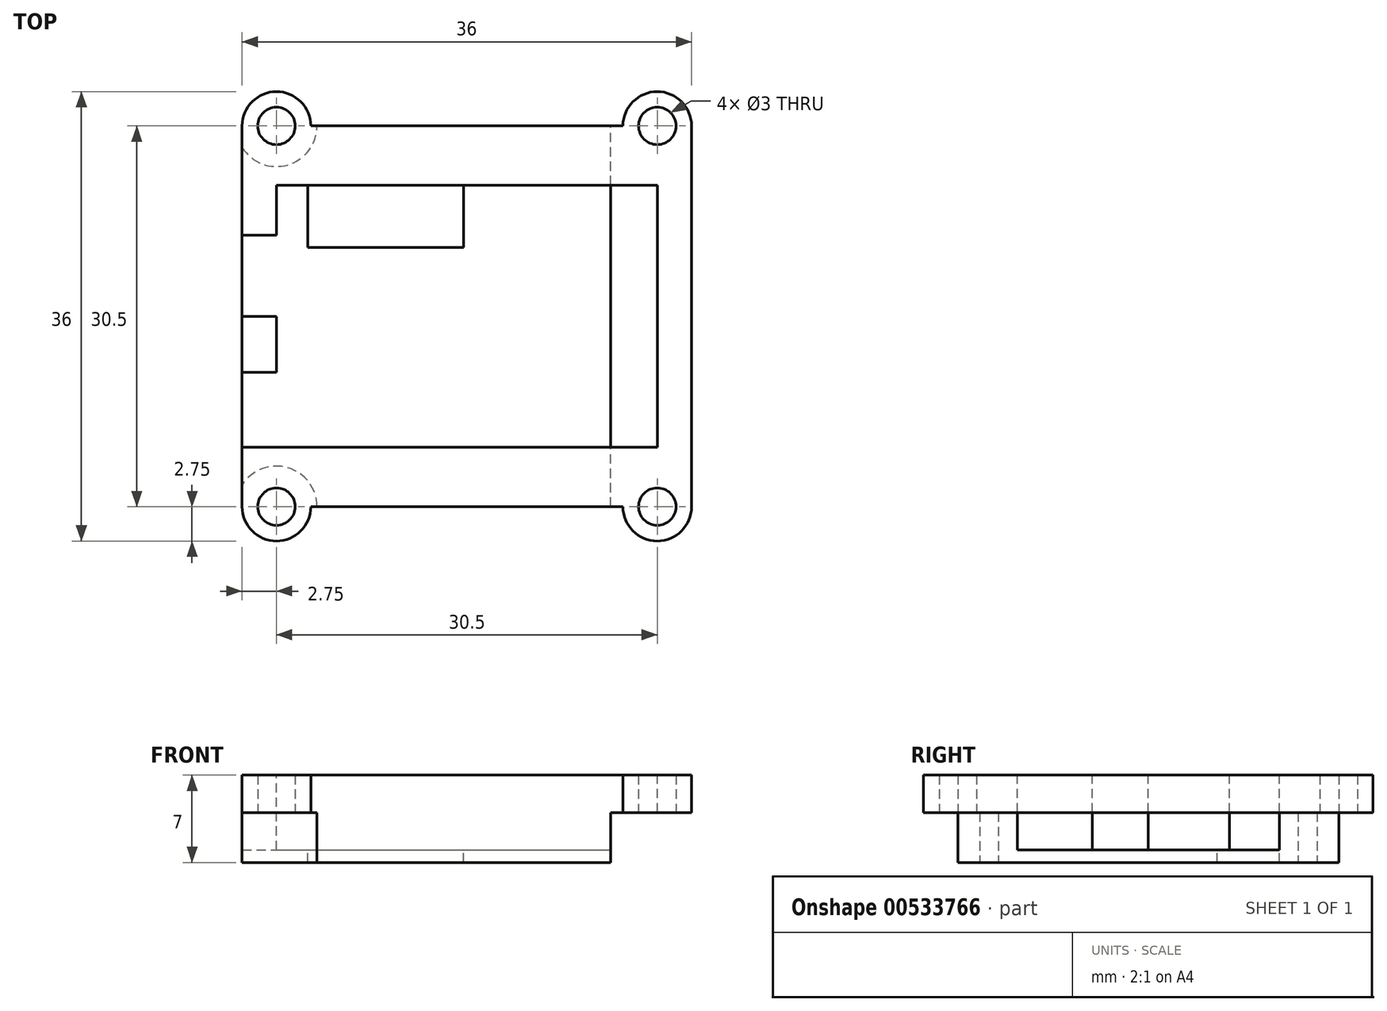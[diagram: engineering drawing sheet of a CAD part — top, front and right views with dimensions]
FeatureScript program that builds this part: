
annotation { "Feature Type Name" : "Feature", "Feature Type Description" : "" }
export const myFeature = defineFeature(function(context is Context, id is Id, definition is map)
    precondition{}
    {
        {
            var Q0;
            Q0=qCreatedBy(makeId("Top.planeOp"),FACE);
            var sketch = newSketch(context, id + "F0", { "sketchPlane" : qUnion([Q0])});
            skLineSegment(sketch, "E0.bottom", {"start": v(-18, -18) * mm, "end": v(18, -18) * mm});
            skLineSegment(sketch, "E0.top", {"start": v(-18, 18) * mm, "end": v(18, 18) * mm});
            skLineSegment(sketch, "E0.left", {"start": v(-18, -18) * mm, "end": v(-18, 18) * mm});
            skLineSegment(sketch, "E0.right", {"start": v(18, -18) * mm, "end": v(18, 18) * mm});
            skPoint(sketch, "E0.middle", {"position": v(0, 0) * mm});
            skSolve(sketch);
        }
        {
            var Q0;
            Q0=makeQuery(id+"F0.imprint","IMPRINT",FACE,{"disambiguationData":[TD([[makeQuery(id+"F0.imprint","IMPRINT",EDGE,{"derivedFrom":sQuery(id+"F0.wireOp",EDGE,"E0.bottom")}),1.0]])]});
            var Q1;
            Q1=qSketchRegion(id+"F2",true);
            extrude(context, id + "F1", {"entities" : qUnion([Q0, Q1]), "depth" : 7 * mm, "offsetDistance" : 25 * mm});
        }
        {
            var Q0;
            Q0=makeQuery(id+"F1.opExtrude","CAP_FACE",FACE,{"disambiguationData":[OSD([sQuery(id+"F0.wireOp",EDGE,"E0.bottom"),sQuery(id+"F0.wireOp",EDGE,"E0.top"),sQuery(id+"F0.wireOp",EDGE,"E0.left"),sQuery(id+"F0.wireOp",EDGE,"E0.right")])],"isStart":false});
            var Q1;
            Q1=makeQuery(id+"F1.opExtrude","CAP_FACE",FACE,{"disambiguationData":[OSD([sQuery(id+"F0.wireOp",EDGE,"E0.bottom"),sQuery(id+"F0.wireOp",EDGE,"E0.top"),sQuery(id+"F0.wireOp",EDGE,"E0.left"),sQuery(id+"F0.wireOp",EDGE,"E0.right")])],"isStart":false});
            var Q2;
            Q2=makeQuery(id+"F1.opExtrude","CAP_FACE",FACE,{"disambiguationData":[OSD([sQuery(id+"F0.wireOp",EDGE,"E0.bottom"),sQuery(id+"F0.wireOp",EDGE,"E0.top"),sQuery(id+"F0.wireOp",EDGE,"E0.left"),sQuery(id+"F0.wireOp",EDGE,"E0.right")])],"isStart":false});
            var Q3;
            Q3=makeQuery(id+"F1.opExtrude","CAP_FACE",FACE,{"disambiguationData":[OSD([sQuery(id+"F0.wireOp",EDGE,"E0.bottom"),sQuery(id+"F0.wireOp",EDGE,"E0.top"),sQuery(id+"F0.wireOp",EDGE,"E0.left"),sQuery(id+"F0.wireOp",EDGE,"E0.right")])],"isStart":false});
            var Q4;
            Q4=makeQuery(id+"F1.opExtrude","CAP_FACE",FACE,{"disambiguationData":[OSD([sQuery(id+"F0.wireOp",EDGE,"E0.bottom"),sQuery(id+"F0.wireOp",EDGE,"E0.top"),sQuery(id+"F0.wireOp",EDGE,"E0.left"),sQuery(id+"F0.wireOp",EDGE,"E0.right")])],"isStart":false});
            var Q5;
            Q5=makeQuery(id+"F1.opExtrude","CAP_FACE",FACE,{"disambiguationData":[OSD([sQuery(id+"F0.wireOp",EDGE,"E0.bottom"),sQuery(id+"F0.wireOp",EDGE,"E0.top"),sQuery(id+"F0.wireOp",EDGE,"E0.left"),sQuery(id+"F0.wireOp",EDGE,"E0.right")])],"isStart":false});
            var Q6;
            Q6=makeQuery(id+"F1.opExtrude","CAP_FACE",FACE,{"disambiguationData":[OSD([sQuery(id+"F0.wireOp",EDGE,"E0.bottom"),sQuery(id+"F0.wireOp",EDGE,"E0.top"),sQuery(id+"F0.wireOp",EDGE,"E0.left"),sQuery(id+"F0.wireOp",EDGE,"E0.right")])],"isStart":false});
            var Q7;
            Q7=makeQuery(id+"F1.opExtrude","CAP_FACE",FACE,{"disambiguationData":[OSD([sQuery(id+"F0.wireOp",EDGE,"E0.bottom"),sQuery(id+"F0.wireOp",EDGE,"E0.top"),sQuery(id+"F0.wireOp",EDGE,"E0.left"),sQuery(id+"F0.wireOp",EDGE,"E0.right")])],"isStart":false});
            var sketch = newSketch(context, id + "F2", { "sketchPlane" : qUnion([Q0, Q1, Q2, Q3, Q4, Q5, Q6, Q7])});
            skLineSegment(sketch, "E1.bottom", {"start": v(-15.25, -10.5) * mm, "end": v(15.25, -10.5) * mm});
            skLineSegment(sketch, "E1.top", {"start": v(-15.25, 10.5) * mm, "end": v(15.25, 10.5) * mm});
            skLineSegment(sketch, "E1.left", {"start": v(-15.25, -10.5) * mm, "end": v(-15.25, 10.5) * mm});
            skLineSegment(sketch, "E1.right", {"start": v(15.25, -10.5) * mm, "end": v(15.25, 10.5) * mm});
            skPoint(sketch, "E1.middle", {"position": v(0, 0) * mm});
            skSolve(sketch);
        }
        {
            var Q0;
            Q0=qSketchRegion(id+"F2",true);
            extrude(context, id + "F3", {"entities" : qUnion([Q0]), "operationType" : NewBodyOperationType.REMOVE, "oppositeDirection" : true, "depth" : 6 * mm, "offsetDistance" : 25 * mm});
        }
        {
            var Q0;
            Q0=makeQuery(id+"F2.imprint","IMPRINT",FACE,{"disambiguationData":[TD([[makeQuery(id+"F2.imprint","IMPRINT",EDGE,{"derivedFrom":sQuery(id+"F2.wireOp",EDGE,"E1.bottom")}),-1.0]])]});
            var Q1;
            Q1=makeQuery(id+"F2.imprint","IMPRINT",FACE,{"disambiguationData":[TD([[makeQuery(id+"F2.imprint","IMPRINT",EDGE,{"derivedFrom":sQuery(id+"F2.wireOp",EDGE,"E1.bottom")}),-1.0]])]});
            var sketch = newSketch(context, id + "F4", { "sketchPlane" : qUnion([Q0, Q1])});
            skLineSegment(sketch, "E2.bottom", {"start": v(-15.25, -10.5) * mm, "end": v(-18, -10.5) * mm});
            skLineSegment(sketch, "E2.top", {"start": v(-15.25, -4.5) * mm, "end": v(-18, -4.5) * mm});
            skLineSegment(sketch, "E2.left", {"start": v(-15.25, -10.5) * mm, "end": v(-15.25, -4.5) * mm});
            skLineSegment(sketch, "E2.right", {"start": v(-18, -10.5) * mm, "end": v(-18, -4.5) * mm});
            skSolve(sketch);
        }
        {
            var Q0;
            Q0=qSketchRegion(id+"F4",true);
            extrude(context, id + "F5", {"entities" : qUnion([Q0]), "operationType" : NewBodyOperationType.REMOVE, "oppositeDirection" : true, "depth" : 6 * mm, "offsetDistance" : 25 * mm});
        }
        {
            var Q0;
            Q0=makeQuery(id+"F2.imprint","IMPRINT",FACE,{"disambiguationData":[TD([[makeQuery(id+"F2.imprint","IMPRINT",EDGE,{"derivedFrom":sQuery(id+"F2.wireOp",EDGE,"E1.bottom")}),-1.0]])]});
            var sketch = newSketch(context, id + "F6", { "sketchPlane" : qUnion([Q0])});
            skLineSegment(sketch, "E3.bottom", {"start": v(-18, 0) * mm, "end": v(-15.25, 0) * mm});
            skLineSegment(sketch, "E3.top", {"start": v(-18, 6.5) * mm, "end": v(-15.25, 6.5) * mm});
            skLineSegment(sketch, "E3.left", {"start": v(-18, 0) * mm, "end": v(-18, 6.5) * mm});
            skLineSegment(sketch, "E3.right", {"start": v(-15.25, 0) * mm, "end": v(-15.25, 6.5) * mm});
            skSolve(sketch);
        }
        {
            var Q0;
            Q0=qSketchRegion(id+"F6",true);
            extrude(context, id + "F7", {"entities" : qUnion([Q0]), "operationType" : NewBodyOperationType.REMOVE, "oppositeDirection" : true, "depth" : 6 * mm, "offsetDistance" : 25 * mm});
        }
        {
            var Q0;
            Q0=makeQuery(id+"F2.imprint","IMPRINT",FACE,{"disambiguationData":[TD([[makeQuery(id+"F2.imprint","IMPRINT",EDGE,{"derivedFrom":sQuery(id+"F2.wireOp",EDGE,"E1.bottom")}),1.0]])]});
            var Q1;
            Q1=qCreatedBy(makeId("Top.planeOp"),FACE);
            var sketch = newSketch(context, id + "F8", { "sketchPlane" : qUnion([Q0, Q1])});
            skLineSegment(sketch, "E4.bottom", {"start": v(-12.75, 10.5) * mm, "end": v(-0.25, 10.5) * mm});
            skLineSegment(sketch, "E4.top", {"start": v(-12.75, 5.5) * mm, "end": v(-0.25, 5.5) * mm});
            skLineSegment(sketch, "E4.left", {"start": v(-12.75, 10.5) * mm, "end": v(-12.75, 5.5) * mm});
            skLineSegment(sketch, "E4.right", {"start": v(-0.25, 10.5) * mm, "end": v(-0.25, 5.5) * mm});
            skSolve(sketch);
        }
        {
            var Q0;
            Q0=qSketchRegion(id+"F8",true);
            extrude(context, id + "F9", {"entities" : qUnion([Q0]), "operationType" : NewBodyOperationType.REMOVE, "oppositeDirection" : true, "depth" : 7 * mm, "offsetDistance" : 25 * mm});
        }
        {
            var Q0;
            Q0=qCreatedBy(makeId("Top.planeOp"),FACE);
            var Q1;
            Q1=qCreatedBy(makeId("Top.planeOp"),FACE);
            var Q2;
            Q2=qCreatedBy(makeId("Top.planeOp"),FACE);
            var Q3;
            Q3=qCreatedBy(makeId("Top.planeOp"),FACE);
            var Q4;
            Q4=qCreatedBy(makeId("Top.planeOp"),FACE);
            var Q5;
            Q5=makeQuery(id+"F2.imprint","IMPRINT",FACE,{"disambiguationData":[TD([[makeQuery(id+"F2.imprint","IMPRINT",EDGE,{"derivedFrom":sQuery(id+"F2.wireOp",EDGE,"E1.bottom")}),-1.0]])]});
            var sketch = newSketch(context, id + "F10", { "sketchPlane" : qUnion([Q0, Q1, Q2, Q3, Q4, Q5])});
            skLineSegment(sketch, "E5.bottom", {"start": v(-15.25, 15.25) * mm, "end": v(15.25, 15.25) * mm});
            skLineSegment(sketch, "E5.left", {"start": v(-15.25, 15.25) * mm, "end": v(-15.25, -15.25) * mm});
            skLineSegment(sketch, "E5.right", {"start": v(15.25, 15.25) * mm, "end": v(15.25, -15.25) * mm});
            skPoint(sketch, "E5.middle", {"position": v(0, 0) * mm});
            skCircle(sketch, "E6", {"center": v(-15.25, 15.25) * mm, "radius": 2.75 * mm});
            skCircle(sketch, "E7", {"center": v(15.25, 15.25) * mm, "radius": 2.75 * mm});
            skCircle(sketch, "E8", {"center": v(15.25, -15.25) * mm, "radius": 2.75 * mm});
            skCircle(sketch, "E9", {"center": v(-15.25, -15.25) * mm, "radius": 2.75 * mm});
            skArc(sketch, "E10", {"start": v(-15.25, 18) * mm, "mid": v(-13.3, 17.2) * mm, "end": v(-12.5, 15.25) * mm});
            skArc(sketch, "E11", {"start": v(-15.25, 18) * mm, "mid": v(-17.2, 17.2) * mm, "end": v(-18, 15.25) * mm});
            skArc(sketch, "E12", {"start": v(15.25, 18) * mm, "mid": v(13.3, 17.2) * mm, "end": v(12.5, 15.25) * mm});
            skArc(sketch, "E13", {"start": v(15.25, 18) * mm, "mid": v(17.2, 17.2) * mm, "end": v(18, 15.25) * mm});
            skArc(sketch, "E14", {"start": v(-15.25, -18) * mm, "mid": v(-17.2, -17.2) * mm, "end": v(-18, -15.25) * mm});
            skArc(sketch, "E15", {"start": v(-12.5, -15.25) * mm, "mid": v(-13.3, -17.2) * mm, "end": v(-15.25, -18) * mm});
            skArc(sketch, "E16", {"start": v(12.54, -15.74) * mm, "mid": v(13.49, -17.36) * mm, "end": v(15.25, -18) * mm});
            skArc(sketch, "E17", {"start": v(18, -15.25) * mm, "mid": v(17.2, -17.2) * mm, "end": v(15.25, -18) * mm});
            skLineSegment(sketch, "E18", {"start": v(-12.5, -15.25) * mm, "end": v(12.54, -15.74) * mm});
            skLineSegment(sketch, "E19", {"start": v(-15.25, -18) * mm, "end": v(15.25, -18) * mm});
            skSolve(sketch);
        }
        {
            var Q0;
            Q0=sQuery(id+"F10.wireOp",VERTEX,"E5.bottom.start");
            var Q1;
            Q1=sQuery(id+"F10.wireOp",VERTEX,"E5.bottom.end");
            var Q2;
            Q2=sQuery(id+"F10.wireOp",VERTEX,"E5.left.end");
            var Q3;
            Q3=sQuery(id+"F10.wireOp",VERTEX,"E5.right.end");
            var Q4;
            Q4=makeQuery(id+"F1.opExtrude","SWEPT_BODY",BODY,{"disambiguationData":[OSD([sQuery(id+"F0.wireOp",EDGE,"E0.bottom"),sQuery(id+"F0.wireOp",EDGE,"E0.top"),sQuery(id+"F0.wireOp",EDGE,"E0.left"),sQuery(id+"F0.wireOp",EDGE,"E0.right")])]});
            hole(context, id + "F11", {"style" : HoleStyle.SIMPLE, "endStyle" : HoleEndStyle.THROUGH, "oppositeDirection" : true, "holeDiameter" : 3 * mm, "isTappedThrough" : true, "tappedDepth" : 12 * mm, "tapClearance" : 3, "locations" : qUnion([Q0, Q1, Q2, Q3]), "scope" : qUnion([Q4])});
        }
        {
            var Q0;
            Q0=qCreatedBy(makeId("Top.planeOp"),FACE);
            var sketch = newSketch(context, id + "F12", { "sketchPlane" : qUnion([Q0])});
            skArc(sketch, "E20", {"start": v(-15.25, 18) * mm, "mid": v(-13.3, 17.2) * mm, "end": v(-12.5, 15.25) * mm});
            skArc(sketch, "E21", {"start": v(15.25, 18) * mm, "mid": v(17.2, 17.2) * mm, "end": v(18, 15.25) * mm});
            skArc(sketch, "E22", {"start": v(18, -15.25) * mm, "mid": v(17.2, -17.2) * mm, "end": v(15.25, -18) * mm});
            skArc(sketch, "E23", {"start": v(-15.25, -18) * mm, "mid": v(-17.2, -17.2) * mm, "end": v(-18, -15.25) * mm});
            skArc(sketch, "E24", {"start": v(-15.25, 18) * mm, "mid": v(-17.2, 17.2) * mm, "end": v(-18, 15.25) * mm});
            skArc(sketch, "E25", {"start": v(15.25, 18) * mm, "mid": v(13.3, 17.2) * mm, "end": v(12.5, 15.25) * mm});
            skArc(sketch, "E26", {"start": v(-15.25, -18) * mm, "mid": v(-13.3, -17.2) * mm, "end": v(-12.5, -15.25) * mm});
            skArc(sketch, "E27", {"start": v(15.25, -18) * mm, "mid": v(13.3, -17.2) * mm, "end": v(12.5, -15.25) * mm});
            skLineSegment(sketch, "E28", {"start": v(-12.5, -15.25) * mm, "end": v(12.5, -15.25) * mm});
            skLineSegment(sketch, "E29", {"start": v(-15.25, -18) * mm, "end": v(15.25, -18) * mm});
            skLineSegment(sketch, "E30", {"start": v(-12.5, 15.25) * mm, "end": v(12.5, 15.25) * mm});
            skLineSegment(sketch, "E31", {"start": v(-15.25, 18) * mm, "end": v(15.25, 18) * mm});
            skLineSegment(sketch, "E32", {"start": v(-15.25, 18) * mm, "end": v(-18.01, 18) * mm});
            skLineSegment(sketch, "E33", {"start": v(-18.01, 18) * mm, "end": v(-18, 15.25) * mm});
            skLineSegment(sketch, "E34", {"start": v(15.25, 18) * mm, "end": v(18, 18) * mm});
            skLineSegment(sketch, "E35", {"start": v(18, 18) * mm, "end": v(18, 15.25) * mm});
            skLineSegment(sketch, "E36", {"start": v(-18, -15.25) * mm, "end": v(-18, -18) * mm});
            skLineSegment(sketch, "E37", {"start": v(-18, -18) * mm, "end": v(-15.25, -18) * mm});
            skLineSegment(sketch, "E38", {"start": v(15.25, -18) * mm, "end": v(18, -18) * mm});
            skLineSegment(sketch, "E39", {"start": v(18, -18) * mm, "end": v(18, -15.25) * mm});
            skSolve(sketch);
        }
        {
            var Q0;
            Q0=qSketchRegion(id+"F12",true);
            var Q1;
            Q1=qSketchRegion(id+"F12",true);
            extrude(context, id + "F13", {"entities" : qUnion([Q0, Q1]), "operationType" : NewBodyOperationType.REMOVE, "depth" : 25 * mm, "offsetDistance" : 25 * mm});
        }
        {
            var Q0;
            Q0=qCreatedBy(makeId("Top.planeOp"),FACE);
            var Q1;
            Q1=qCreatedBy(makeId("Top.planeOp"),FACE);
            var Q2;
            Q2=qCreatedBy(makeId("Top.planeOp"),FACE);
            var sketch = newSketch(context, id + "F14", { "sketchPlane" : qUnion([Q0, Q1, Q2])});
            skCircle(sketch, "E40", {"center": v(-15.25, -15.25) * mm, "radius": 3.25 * mm});
            skCircle(sketch, "E41", {"center": v(15.25, -15.25) * mm, "radius": 3.25 * mm});
            skCircle(sketch, "E42", {"center": v(-15.25, 15.25) * mm, "radius": 3.25 * mm});
            skCircle(sketch, "E43", {"center": v(15.25, 15.25) * mm, "radius": 3.25 * mm});
            skSolve(sketch);
        }
        {
            var Q0;
            Q0=qSketchRegion(id+"F14",true);
            extrude(context, id + "F15", {"entities" : qUnion([Q0]), "operationType" : NewBodyOperationType.REMOVE, "depth" : 4 * mm, "offsetDistance" : 25 * mm});
        }
        {
            var Q0;
            Q0=qCreatedBy(makeId("Top.planeOp"),FACE);
            var Q1;
            Q1=qCreatedBy(makeId("Top.planeOp"),FACE);
            var sketch = newSketch(context, id + "F16", { "sketchPlane" : qUnion([Q0, Q1])});
            skLineSegment(sketch, "E44.bottom", {"start": v(18, -18) * mm, "end": v(11.5, -18) * mm});
            skLineSegment(sketch, "E44.top", {"start": v(18, 18) * mm, "end": v(11.5, 18) * mm});
            skLineSegment(sketch, "E44.left", {"start": v(18, -18) * mm, "end": v(18, 18) * mm});
            skLineSegment(sketch, "E44.right", {"start": v(11.5, -18) * mm, "end": v(11.5, 18) * mm});
            skSolve(sketch);
        }
        {
            var Q0;
            Q0=qSketchRegion(id+"F16",true);
            extrude(context, id + "F17", {"entities" : qUnion([Q0]), "operationType" : NewBodyOperationType.REMOVE, "depth" : 4 * mm, "offsetDistance" : 25 * mm});
        }
    });
